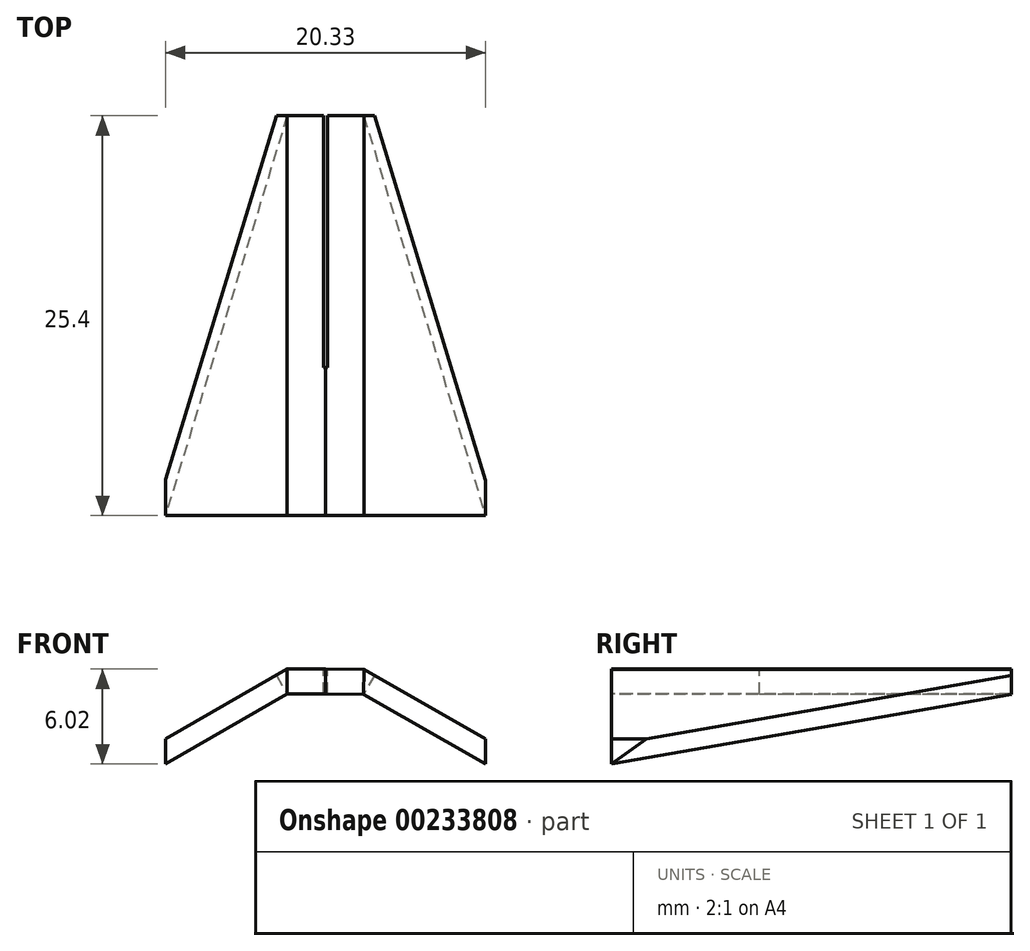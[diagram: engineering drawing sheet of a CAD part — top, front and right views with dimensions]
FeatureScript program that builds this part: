
annotation { "Feature Type Name" : "Feature", "Feature Type Description" : "" }
export const myFeature = defineFeature(function(context is Context, id is Id, definition is map)
    precondition{}
    {
        {
            var Q0;
            Q0=qCreatedBy(makeId("Front.planeOp"),FACE);
            var sketch = newSketch(context, id + "F0", { "sketchPlane" : qUnion([Q0])});
            skLineSegment(sketch, "E0", {"start": v(-10.16, 0) * mm, "end": v(-2.44, 4.43) * mm});
            skLineSegment(sketch, "E1", {"start": v(2.43, 4.41) * mm, "end": v(10.16, 0) * mm});
            skLineSegment(sketch, "E2", {"start": v(-2.44, 4.43) * mm, "end": v(0, 4.43) * mm});
            skLineSegment(sketch, "E3", {"start": v(0, 4.43) * mm, "end": v(2.43, 4.41) * mm});
            skSolve(sketch);
        }
        {
            var Q0;
            Q0=sQuery(id+"F0.wireOp",EDGE,"E0");
            var Q1;
            Q1=sQuery(id+"F0.wireOp",EDGE,"E2");
            var Q2;
            Q2=sQuery(id+"F0.wireOp",EDGE,"E3");
            var Q3;
            Q3=sQuery(id+"F0.wireOp",EDGE,"E1");
            extrude(context, id + "F1", {"bodyType" : ToolBodyType.SURFACE, "surfaceEntities" : qUnion([Q0, Q1, Q2, Q3]), "depth" : 25.4 * mm});
        }
        {
            var Q0;
            Q0=makeQuery(id+"F1.opExtrude","SWEPT_FACE",FACE,{"disambiguationData":[OSD([sQuery(id+"F0.wireOp",EDGE,"E3")])]});
            var Q1;
            Q1=makeQuery(id+"F1.opExtrude","SWEPT_FACE",FACE,{"disambiguationData":[OSD([sQuery(id+"F0.wireOp",EDGE,"E2")])]});
            var Q2;
            Q2=makeQuery(id+"F1.opExtrude","SWEPT_FACE",FACE,{"disambiguationData":[OSD([sQuery(id+"F0.wireOp",EDGE,"E1")])]});
            var Q3;
            Q3=makeQuery(id+"F1.opExtrude","SWEPT_FACE",FACE,{"disambiguationData":[OSD([sQuery(id+"F0.wireOp",EDGE,"E0")])]});
            extrude(context, id + "F2", {"entities" : qUnion([Q0, Q1, Q2, Q3]), "depth" : 1.59 * mm});
        }
        {
            var Q0;
            Q0=makeQuery(id+"F1.opExtrude","SWEPT_FACE",FACE,{"disambiguationData":[OSD([sQuery(id+"F0.wireOp",EDGE,"E3")])]});
            var sketch = newSketch(context, id + "F3", { "sketchPlane" : qUnion([Q0])});
            skLineSegment(sketch, "E4", {"start": v(-0.16, 0) * mm, "end": v(-0.16, 16) * mm});
            skLineSegment(sketch, "E5", {"start": v(-0.16, 16) * mm, "end": v(-0.03, 16) * mm});
            skLineSegment(sketch, "E6", {"start": v(-0.03, 16) * mm, "end": v(0.1, 16) * mm});
            skLineSegment(sketch, "E7", {"start": v(0.1, 16) * mm, "end": v(0.1, 0) * mm});
            skLineSegment(sketch, "E8", {"start": v(-0.16, 0) * mm, "end": v(-0.03, 0) * mm});
            skLineSegment(sketch, "E9", {"start": v(-0.03, 0) * mm, "end": v(0.1, 0) * mm});
            skSolve(sketch);
        }
        {
            var Q0;
            {var subQ3=sQuery(id+"F3.wireOp",EDGE,"E7");Q0=makeQuery(id+"F3.imprint","IMPRINT",FACE,{"disambiguationData":[TD([[makeQuery(id+"F3.imprint","IMPRINT",EDGE,{"derivedFrom":subQ3}),-1.0]])]});}
            var Q1;
            Q1=makeQuery(id+"F3.imprint","IMPRINT",FACE,{"disambiguationData":[TD([[makeQuery(id+"F3.imprint","IMPRINT",EDGE,{"derivedFrom":sQuery(id+"F3.wireOp",EDGE,"E4")}),-1.0]])]});
            extrude(context, id + "F4", {"entities" : qUnion([Q0, Q1]), "operationType" : NewBodyOperationType.REMOVE, "depth" : 6.1 * mm});
        }
        {
            var Q0;
            Q0=makeQuery(id+"F2.opExtrude","CAP_FACE",FACE,{"disambiguationData":[OSD([sQuery(id+"F0.wireOp",EDGE,"E0")]),OD(0.0)],"isStart":false});
            var sketch = newSketch(context, id + "F5", { "sketchPlane" : qUnion([Q0])});
            skLineSegment(sketch, "E10", {"start": v(-0.71, 0) * mm, "end": v(-9.61, 25.4) * mm});
            skLineSegment(sketch, "E11", {"start": v(-9.61, 25.4) * mm, "end": v(-9.61, 0) * mm});
            skLineSegment(sketch, "E12", {"start": v(-9.61, 0) * mm, "end": v(-0.71, 0) * mm});
            skSolve(sketch);
        }
        {
            var Q0;
            Q0=makeQuery(id+"F5.imprint","IMPRINT",FACE,{"disambiguationData":[TD([[makeQuery(id+"F5.imprint","IMPRINT",EDGE,{"derivedFrom":sQuery(id+"F5.wireOp",EDGE,"E10")}),1.0]])]});
            extrude(context, id + "F6", {"entities" : qUnion([Q0]), "operationType" : NewBodyOperationType.REMOVE, "oppositeDirection" : true, "depth" : 2.64 * mm});
        }
        {
            var Q0;
            Q0=makeQuery(id+"F2.opExtrude","CAP_FACE",FACE,{"disambiguationData":[OSD([sQuery(id+"F0.wireOp",EDGE,"E1")]),OD(0.0)],"isStart":false});
            var sketch = newSketch(context, id + "F7", { "sketchPlane" : qUnion([Q0])});
            skLineSegment(sketch, "E13", {"start": v(0.7, 0) * mm, "end": v(9.6, 25.4) * mm});
            skLineSegment(sketch, "E14", {"start": v(9.6, 25.4) * mm, "end": v(9.6, 0) * mm});
            skLineSegment(sketch, "E15", {"start": v(9.6, 0) * mm, "end": v(0.7, 0) * mm});
            skSolve(sketch);
        }
        {
            var Q0;
            Q0=makeQuery(id+"F7.imprint","IMPRINT",FACE,{"disambiguationData":[TD([[makeQuery(id+"F7.imprint","IMPRINT",EDGE,{"derivedFrom":sQuery(id+"F7.wireOp",EDGE,"E13")}),-1.0]])]});
            extrude(context, id + "F8", {"entities" : qUnion([Q0]), "operationType" : NewBodyOperationType.REMOVE, "oppositeDirection" : true, "depth" : 25.4 * mm});
        }
    });
